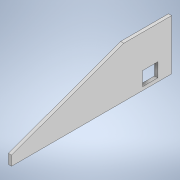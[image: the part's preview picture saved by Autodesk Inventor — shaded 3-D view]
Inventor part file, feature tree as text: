
AUTODESK INVENTOR PART (.ipt)
format: ipt  version: 2021 (Build 250183000, 183)  size: 110,080 bytes
history: native  units: in
note: dims shown in document units (in); Inventor stores cm internally (conversion verified against a paired STEP export)
features: extrude x2, sketch x2
ambient origin geometry x8: Origin, YZ Plane, XZ Plane, XY Plane, X Axis, Y Axis, Z Axis, Center Point
bodies: Solid1 (feature_tree)
feature tree (4):
  extrude  "Extrusion1"  Depth=0.1in TaperAngle=0.0deg
  extrude  "Extrusion2"  Depth=0.433in
  sketch  "Sketch1"  dims[d1=3.75in d2=0.1in d3=0.0in]
  sketch  "Sketch2"  dims[d4=0.1374in d5=0.3in d6=1.5in d7=0.48in d8=0.436in d9=0.1in d10=0.0in d11=0.109in d12=0.433in]
